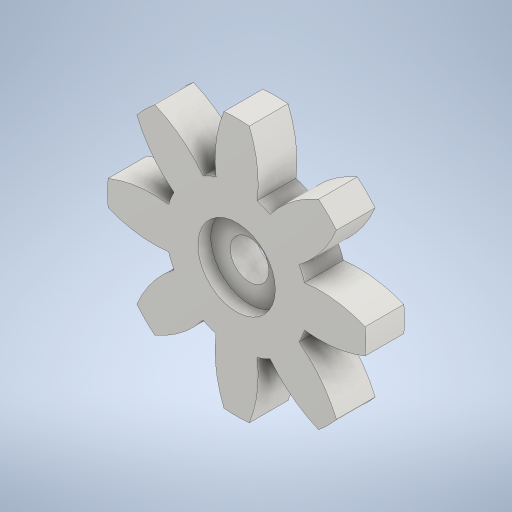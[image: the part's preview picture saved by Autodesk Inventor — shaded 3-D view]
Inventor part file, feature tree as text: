
AUTODESK INVENTOR PART (.ipt)
format: ipt  version: 2023.2 (Build 272271030, 271C)  size: 718,336 bytes
history: native  units: mm (DEFAULTED — no unit token found)
features: sketch x4, extrude x3, plane x3, other x3
ambient origin geometry x8: Origin, YZ Plane, XZ Plane, XY Plane, X Axis, Y Axis, Z Axis, Center Point
bodies: Solid1 (feature_tree)
feature tree (13):
  extrude  "Extrusion1"  Depth=3.0mm TaperAngle=0.0deg
  plane  "Work Plane2"
  plane  "Work Plane8"
  plane  "Work Plane9"
  other  "Spur Gear"
  extrude  "Extrusion2"  Depth=10.0mm TaperAngle=0.0deg
  extrude  "Extrusion3"  TaperAngle=0.0deg  [1 undecoded]
  sketch  "Sketch1"  dims[d0=20.0mm d1=3.0mm d2=0.0mm]
  sketch  "Sketch2"  dims[d3=16.0mm d4=10.0mm d5=0.0mm]
  other  "Srf1"
  sketch  "Sketch3"  dims[d16=24.0mm d17=0.0mm d34=22.5deg]
  sketch  "Sketch4"  dims[d39=0.0mm d41=0.0mm d43=24.0mm d46=24.0mm d47=0.0mm d48=0.0mm d49=6.0mm d50=1.0mm d51=0.0mm d52=3.0mm d53=2.0mm d54=0.0mm d55=0.5mm d56=0.872665mm d57=0.5mm d58=0.872665mm]
  other  "Pitch Diameter"
note: 1 required parameter value undecoded (feature->parameter linkage not recoverable at this tier; creation-order binding heuristic only, values carry confidence <= 0.55)
